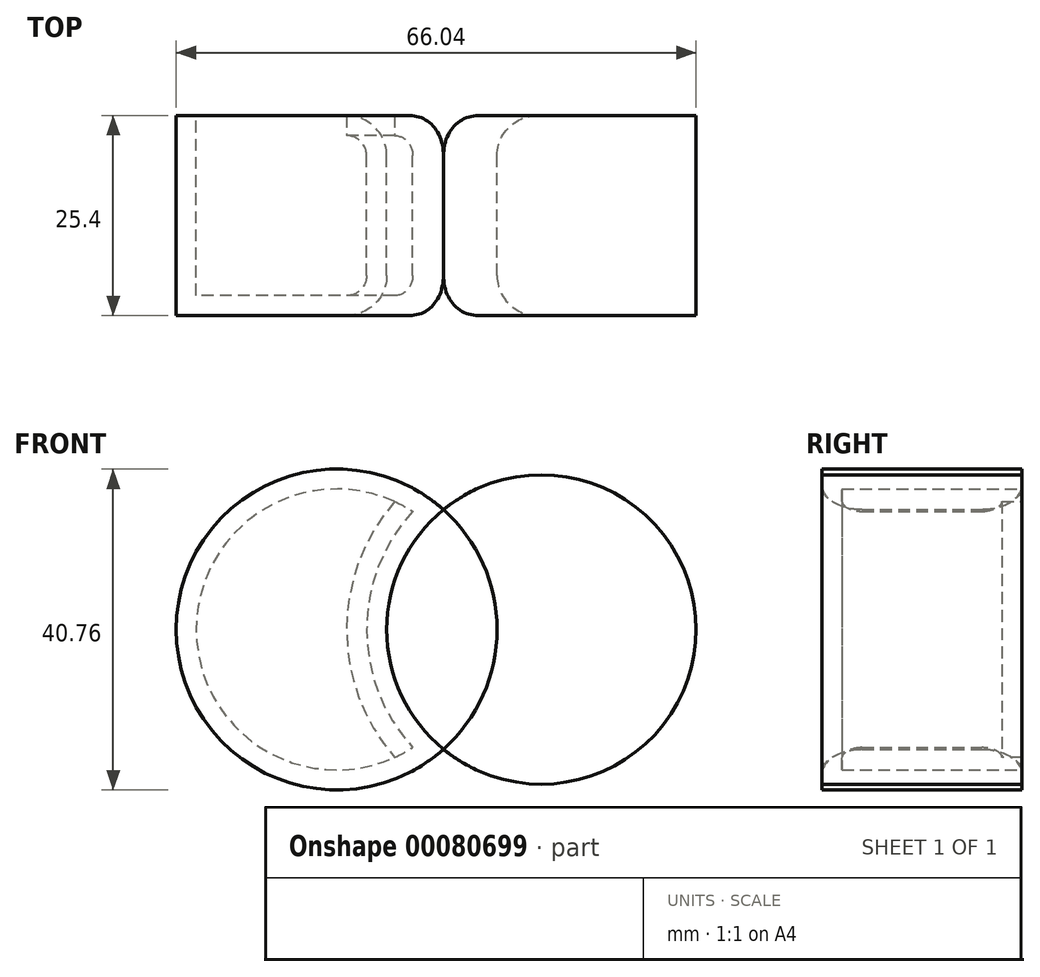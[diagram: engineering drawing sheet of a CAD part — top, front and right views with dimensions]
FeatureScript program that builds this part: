
annotation { "Feature Type Name" : "Feature", "Feature Type Description" : "" }
export const myFeature = defineFeature(function(context is Context, id is Id, definition is map)
    precondition{}
    {
        {
            var Q0;
            Q0=qCreatedBy(makeId("Front.planeOp"),FACE);
            var sketch = newSketch(context, id + "F0", { "sketchPlane" : qUnion([Q0])});
            skCircle(sketch, "E0", {"center": v(0, 0) * mm, "radius": 19.65 * mm});
            skCircle(sketch, "E1", {"center": v(-26, 0) * mm, "radius": 20.38 * mm});
            skSolve(sketch);
        }
        {
            var Q0;
            {var subQ0=sQuery(id+"F0.wireOp",EDGE,"E1");var subQ1=sQuery(id+"F0.wireOp",EDGE,"E0");var subQ2=makeQuery(id+"F0.imprint","INTERSECT",VERTEX,{"disambiguationData":[OD(0.0)],"derivedFrom":[subQ1,subQ0]});Q0=makeQuery(id+"F0.imprint","IMPRINT",FACE,{"disambiguationData":[TD([[makeQuery(id+"F0.imprint","IMPRINT",EDGE,{"disambiguationData":[TD([[subQ2,1.0]])],"derivedFrom":subQ1}),-1.0]])]});}
            var Q1;
            {var subQ0=sQuery(id+"F0.wireOp",EDGE,"E1");var subQ1=sQuery(id+"F0.wireOp",EDGE,"E0");var subQ2=makeQuery(id+"F0.imprint","INTERSECT",VERTEX,{"disambiguationData":[OD(0.0)],"derivedFrom":[subQ1,subQ0]});Q1=makeQuery(id+"F0.imprint","IMPRINT",FACE,{"disambiguationData":[TD([[makeQuery(id+"F0.imprint","IMPRINT",EDGE,{"disambiguationData":[TD([[subQ2,-1.0]])],"derivedFrom":subQ1}),1.0]])]});}
            extrude(context, id + "F1", {"entities" : qUnion([Q0, Q1]), "depth" : 25.4 * mm});
        }
        {
            var Q0;
            {var subQ0=sQuery(id+"F0.wireOp",EDGE,"E1");var subQ1=sQuery(id+"F0.wireOp",EDGE,"E0");Q0=makeQuery(id+"F1.opExtrude","CAP_EDGE",EDGE,{"disambiguationData":[OSD([subQ0]),TDD([makeQuery(id+"F0.imprint","IMPRINT",EDGE,{"disambiguationData":[TD([[makeQuery(id+"F0.imprint","INTERSECT",VERTEX,{"disambiguationData":[OD(0.0)],"derivedFrom":[subQ1,subQ0]}),-1.0]])],"derivedFrom":subQ0})])],"isStart":false});}
            var Q1;
            {var subQ0=sQuery(id+"F0.wireOp",EDGE,"E1");var subQ1=sQuery(id+"F0.wireOp",EDGE,"E0");Q1=makeQuery(id+"F1.opExtrude","CAP_EDGE",EDGE,{"disambiguationData":[OSD([subQ1]),TDD([makeQuery(id+"F0.imprint","IMPRINT",EDGE,{"disambiguationData":[TD([[makeQuery(id+"F0.imprint","INTERSECT",VERTEX,{"disambiguationData":[OD(0.0)],"derivedFrom":[subQ1,subQ0]}),1.0]])],"derivedFrom":subQ1})])],"isStart":false});}
            var Q2;
            {var subQ0=sQuery(id+"F0.wireOp",EDGE,"E1");var subQ1=sQuery(id+"F0.wireOp",EDGE,"E0");Q2=makeQuery(id+"F1.opExtrude","CAP_EDGE",EDGE,{"disambiguationData":[OSD([subQ1]),TDD([makeQuery(id+"F0.imprint","IMPRINT",EDGE,{"disambiguationData":[TD([[makeQuery(id+"F0.imprint","INTERSECT",VERTEX,{"disambiguationData":[OD(0.0)],"derivedFrom":[subQ1,subQ0]}),1.0]])],"derivedFrom":subQ1})])],"isStart":true});}
            var Q3;
            {var subQ0=sQuery(id+"F0.wireOp",EDGE,"E1");var subQ1=sQuery(id+"F0.wireOp",EDGE,"E0");Q3=makeQuery(id+"F1.opExtrude","CAP_EDGE",EDGE,{"disambiguationData":[OSD([subQ0]),TDD([makeQuery(id+"F0.imprint","IMPRINT",EDGE,{"disambiguationData":[TD([[makeQuery(id+"F0.imprint","INTERSECT",VERTEX,{"disambiguationData":[OD(0.0)],"derivedFrom":[subQ1,subQ0]}),-1.0]])],"derivedFrom":subQ0})])],"isStart":true});}
            fillet(context, id + "F2", {"entities" : qUnion([Q0, Q1, Q2, Q3]), "radius" : 5.08 * mm, "tangentPropagation" : true, "allowEdgeOverflow" : false});
        }
        {
            var Q0;
            {var subQ0=sQuery(id+"F0.wireOp",EDGE,"E1");var subQ1=sQuery(id+"F0.wireOp",EDGE,"E0");var subQ2=makeQuery(id+"F0.imprint","INTERSECT",VERTEX,{"disambiguationData":[OD(0.0)],"derivedFrom":[subQ1,subQ0]});Q0=makeQuery(id+"F1.opExtrude","CAP_FACE",FACE,{"disambiguationData":[OSD([subQ1,subQ0]),TDD([makeQuery(id+"F0.imprint","IMPRINT",EDGE,{"disambiguationData":[TD([[subQ2,1.0]])],"derivedFrom":subQ1}),makeQuery(id+"F0.imprint","IMPRINT",EDGE,{"disambiguationData":[TD([[subQ2,1.0]])],"derivedFrom":subQ0})])],"isStart":true});}
            shell(context, id + "F3", {"entities" : qUnion([Q0]), "thickness" : 2.54 * mm});
        }
    });
